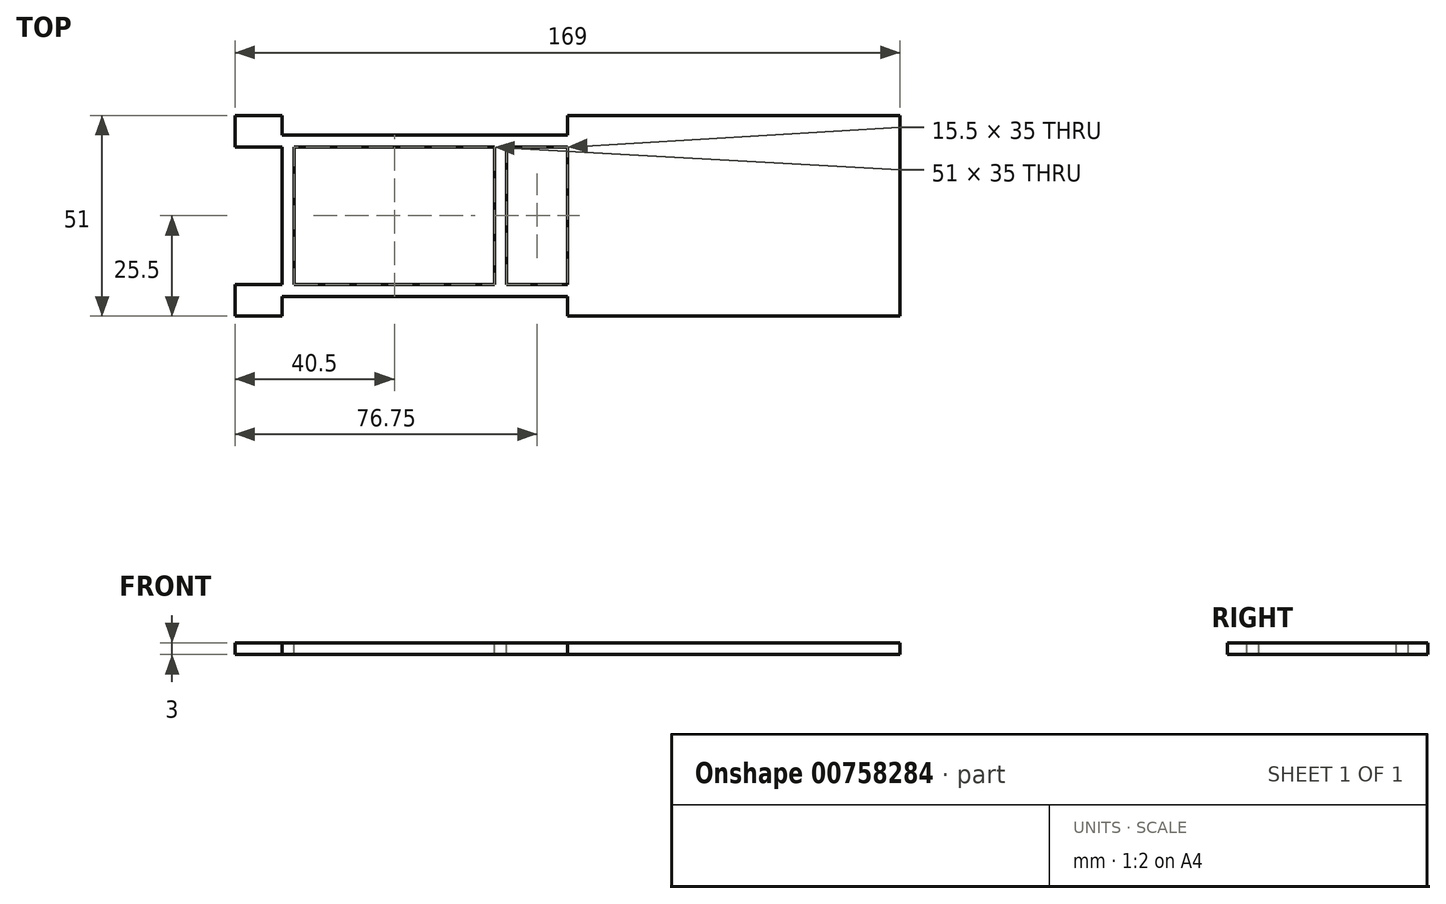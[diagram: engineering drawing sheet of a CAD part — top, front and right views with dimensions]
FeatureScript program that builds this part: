
annotation { "Feature Type Name" : "Feature", "Feature Type Description" : "" }
export const myFeature = defineFeature(function(context is Context, id is Id, definition is map)
    precondition{}
    {
        {
            var Q0;
            Q0=qCreatedBy(makeId("Top.planeOp"),FACE);
            var sketch = newSketch(context, id + "F0", { "sketchPlane" : qUnion([Q0])});
            skLineSegment(sketch, "E0.bottom", {"start": v(84.5, 25.5) * mm, "end": v(-84.5, 25.5) * mm});
            skLineSegment(sketch, "E0.top", {"start": v(84.5, -25.5) * mm, "end": v(-84.5, -25.5) * mm});
            skLineSegment(sketch, "E0.left", {"start": v(84.5, 25.5) * mm, "end": v(84.5, -25.5) * mm});
            skLineSegment(sketch, "E0.right", {"start": v(-84.5, 25.5) * mm, "end": v(-84.5, -25.5) * mm});
            skPoint(sketch, "E0.middle", {"position": v(0, 0) * mm});
            skPoint(sketch, "E1.middle.positionSnap0", {"position": v(-84.5, 0) * mm});
            skPoint(sketch, "E1.centerSnap0", {"position": v(-84.5, 0) * mm});
            skSolve(sketch);
        }
        {
            var Q0;
            Q0=makeQuery(id+"F0.imprint","IMPRINT",FACE,{"disambiguationData":[TD([[makeQuery(id+"F0.imprint","IMPRINT",EDGE,{"derivedFrom":sQuery(id+"F0.wireOp",EDGE,"E0.bottom")}),1.0]])]});
            extrude(context, id + "F1", {"entities" : qUnion([Q0]), "depth" : 3 * mm, "offsetDistance" : 25 * mm});
        }
        {
            var Q0;
            Q0=makeQuery(id+"F1.opExtrude","CAP_FACE",FACE,{"disambiguationData":[OSD([sQuery(id+"F0.wireOp",EDGE,"E0.bottom"),sQuery(id+"F0.wireOp",EDGE,"E0.top"),sQuery(id+"F0.wireOp",EDGE,"E0.left"),sQuery(id+"F0.wireOp",EDGE,"E0.right")])],"isStart":false});
            var sketch = newSketch(context, id + "F2", { "sketchPlane" : qUnion([Q0])});
            skLineSegment(sketch, "E2.bottom", {"start": v(-18.5, 17.5) * mm, "end": v(-69.5, 17.5) * mm});
            skLineSegment(sketch, "E2.top", {"start": v(-18.5, -17.5) * mm, "end": v(-69.5, -17.5) * mm});
            skLineSegment(sketch, "E2.left", {"start": v(-18.5, 17.5) * mm, "end": v(-18.5, -17.5) * mm});
            skLineSegment(sketch, "E2.right", {"start": v(-69.5, 17.5) * mm, "end": v(-69.5, -17.5) * mm});
            skPoint(sketch, "E2.middle", {"position": v(-44, 0) * mm});
            skLineSegment(sketch, "E3.bottom", {"start": v(-84.5, 17.5) * mm, "end": v(-72.5, 17.5) * mm});
            skLineSegment(sketch, "E3.top", {"start": v(-84.5, -17.5) * mm, "end": v(-72.5, -17.5) * mm});
            skLineSegment(sketch, "E3.left", {"start": v(-84.5, 17.5) * mm, "end": v(-84.5, -17.5) * mm});
            skLineSegment(sketch, "E3.right", {"start": v(-72.5, 17.5) * mm, "end": v(-72.5, -17.5) * mm});
            skLineSegment(sketch, "E4.bottom", {"start": v(-72.5, 25.5) * mm, "end": v(0, 25.5) * mm});
            skLineSegment(sketch, "E4.top", {"start": v(-72.5, 20.5) * mm, "end": v(0, 20.5) * mm});
            skLineSegment(sketch, "E4.left", {"start": v(-72.5, 25.5) * mm, "end": v(-72.5, 20.5) * mm});
            skLineSegment(sketch, "E4.right", {"start": v(0, 25.5) * mm, "end": v(0, 20.5) * mm});
            skLineSegment(sketch, "E5.bottom", {"start": v(-72.5, -25.5) * mm, "end": v(0, -25.5) * mm});
            skLineSegment(sketch, "E5.top", {"start": v(-72.5, -20.5) * mm, "end": v(0, -20.5) * mm});
            skLineSegment(sketch, "E5.left", {"start": v(-72.5, -25.5) * mm, "end": v(-72.5, -20.5) * mm});
            skLineSegment(sketch, "E5.right", {"start": v(0, -25.5) * mm, "end": v(0, -20.5) * mm});
            skLineSegment(sketch, "E6.bottom", {"start": v(0, 17.5) * mm, "end": v(-15.5, 17.5) * mm});
            skLineSegment(sketch, "E6.top", {"start": v(0, -17.5) * mm, "end": v(-15.5, -17.5) * mm});
            skLineSegment(sketch, "E6.left", {"start": v(0, 17.5) * mm, "end": v(0, -17.5) * mm});
            skLineSegment(sketch, "E6.right", {"start": v(-15.5, 17.5) * mm, "end": v(-15.5, -17.5) * mm});
            skSolve(sketch);
        }
        {
            var Q0;
            Q0 = qSketchRegion(id + "F2", true);
            var Q1;
            Q1=makeQuery(id+"F1.opExtrude","CAP_FACE",FACE,{"disambiguationData":[OSD([sQuery(id+"F0.wireOp",EDGE,"E0.bottom"),sQuery(id+"F0.wireOp",EDGE,"E0.top"),sQuery(id+"F0.wireOp",EDGE,"E0.left"),sQuery(id+"F0.wireOp",EDGE,"E0.right")])],"isStart":true});
            extrude(context, id + "F3", {"entities" : qUnion([Q0]), "operationType" : NewBodyOperationType.REMOVE, "endBound" : BoundingType.UP_TO_SURFACE, "oppositeDirection" : true, "depth" : 25 * mm, "endBoundEntityFace" : qUnion([Q1]), "offsetDistance" : 25 * mm});
        }
    });
